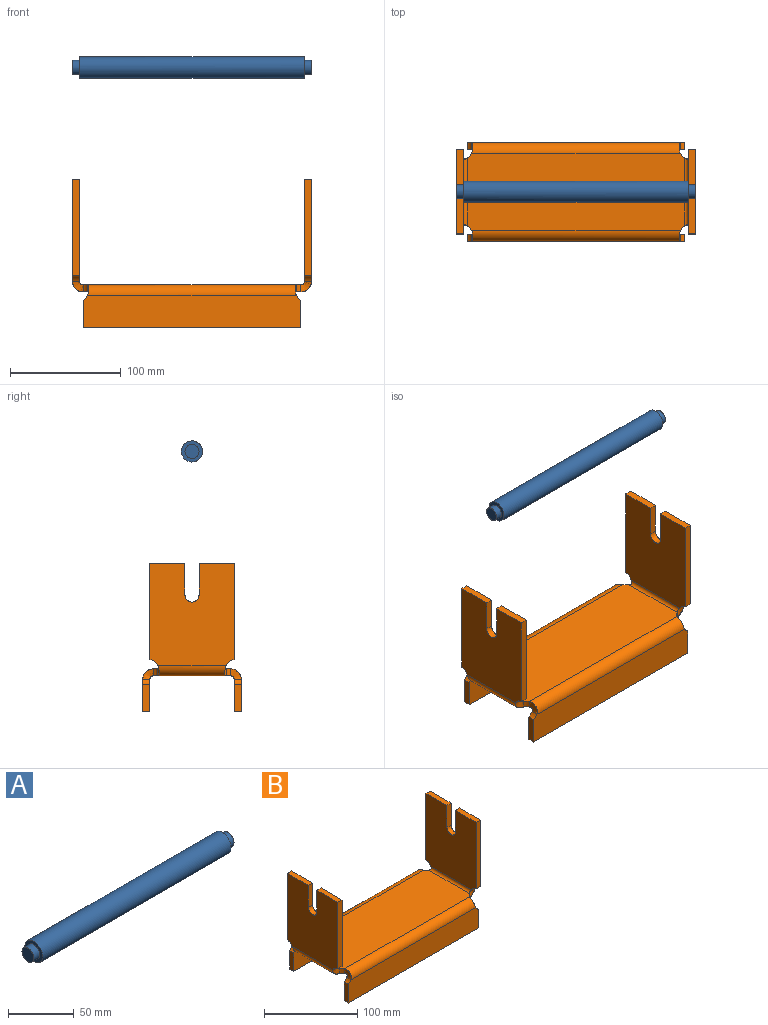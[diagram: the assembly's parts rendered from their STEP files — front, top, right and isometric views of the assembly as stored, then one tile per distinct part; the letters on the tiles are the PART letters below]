
ASSEMBLY  parts=2 mates=3
PART A: 7 faces, bbox 215.9x19.1x19.1 mm
  f0: cylinder r=6.35mm len=12.7mm, axis (-1,0,0), area 253.4mm2, adj f1,f2
  f1: plane 12.7x12.7mm, normal (1,0,0), area 126.7mm2, adj f0
  f2: plane 19.05x19.05mm, normal (1,0,0), area 158.3mm2, adj f0,f4
  f3: plane 19.05x19.05mm, normal (-1,0,0), area 158.3mm2, adj f4,f6
  f4: cylinder r=9.53mm len=203.2mm, axis (-1,0,0), area 12161mm2, adj f2,f3
  f5: plane 12.7x12.7mm, normal (-1,0,0), area 126.7mm2, adj f6
  f6: cylinder r=6.35mm len=12.7mm, axis (-1,0,0), area 253.4mm2, adj f3,f5
PART B: 58 faces, bbox 215.9x88.9x133.4 mm
  f0: plane 31.75x6.35mm, normal (0,0,1), area 201.6mm2, adj f8,f10,f12,f55
  f1: plane 31.75x6.35mm, normal (0,0,1), area 201.6mm2, adj f20,f21,f23,f54
  f2: plane 196.85x69.85mm, normal (0,0,-1), area 13709.2mm2, adj f4,f5,f6,f7,f17,f28,f40,f51
  f3: plane 196.85x69.85mm, normal (0,0,1), area 13709.2mm2, adj f4,f5,f6,f7,f18,f29,f39,f50
  f4: cylinder r=10.05mm len=6.35mm, axis (0,0,1), area 37.6mm2, adj f2,f3,f16,f38
  f5: cylinder r=10.05mm len=6.35mm, axis (0,0,1), area 37.6mm2, adj f2,f3,f27,f37
  f6: cylinder r=10.05mm len=6.35mm, axis (0,0,1), area 37.6mm2, adj f2,f3,f26,f49
  f7: cylinder r=10.05mm len=6.35mm, axis (0,0,1), area 37.6mm2, adj f2,f3,f15,f48
  f8: plane 86.88x6.35mm, normal (0,1,0), area 551.7mm2, adj f0,f10,f12,f13
  f9: plane 86.88x6.35mm, normal (0,-1,0), area 551.7mm2, adj f10,f11,f12,f14
  f10: plane 92.08x76.2mm, normal (-1,0,0), area 6539.3mm2, adj f0,f8,f9,f11,f13,f14,f17,f55
  f11: plane 31.75x6.35mm, normal (0,0,1), area 201.6mm2, adj f9,f10,f12,f56
  f12: plane 92.08x76.2mm, normal (1,0,0), area 6539.3mm2, adj f0,f8,f9,f11,f13,f14,f18,f55
  f13: cylinder r=10.05mm len=7.3mm, axis (1,0,0), area 59mm2, adj f8,f10,f12,f16
  f14: cylinder r=10.05mm len=7.3mm, axis (1,0,0), area 59mm2, adj f9,f10,f12,f15
  f15: bspline ~9.53x9.53mm, area 65.9mm2, adj f7,f14,f17,f18
  f16: bspline ~9.53x9.53mm, area 65.9mm2, adj f4,f13,f17,f18
  f17: cylinder r=9.53mm len=61.6mm, axis (0,-1,0), area 897.6mm2, adj f2,f10,f15,f16
  f18: cylinder r=3.17mm len=61.6mm, axis (0,-1,0), area 299.2mm2, adj f3,f12,f15,f16
  f19: plane 86.88x6.35mm, normal (0,-1,0), area 551.7mm2, adj f21,f22,f23,f24
  f20: plane 86.88x6.35mm, normal (0,1,0), area 551.7mm2, adj f1,f21,f23,f25
  f21: plane 92.08x76.2mm, normal (1,0,0), area 6539.3mm2, adj f1,f19,f20,f22,f24,f25,f28,f52
  f22: plane 31.75x6.35mm, normal (0,0,1), area 201.6mm2, adj f19,f21,f23,f53
  f23: plane 92.08x76.2mm, normal (-1,0,0), area 6539.3mm2, adj f1,f19,f20,f22,f24,f25,f29,f52
  f24: cylinder r=10.05mm len=7.3mm, axis (-1,0,0), area 59mm2, adj f19,f21,f23,f26
  f25: cylinder r=10.05mm len=7.3mm, axis (-1,0,0), area 59mm2, adj f20,f21,f23,f27
  f26: bspline ~9.53x9.53mm, area 65.9mm2, adj f6,f24,f28,f29
  f27: bspline ~9.53x9.53mm, area 65.9mm2, adj f5,f25,f28,f29
  f28: cylinder r=9.53mm len=61.6mm, axis (0,-1,0), area 897.6mm2, adj f2,f21,f26,f27
  f29: cylinder r=3.17mm len=61.6mm, axis (0,-1,0), area 299.2mm2, adj f3,f23,f26,f27
  f30: plane 24.45x6.35mm, normal (1,0,0), area 155.3mm2, adj f32,f33,f34,f35
  f31: plane 24.45x6.35mm, normal (-1,0,0), area 155.3mm2, adj f32,f33,f34,f36
  f32: plane 196.85x28.58mm, normal (0,-1,0), area 5604.6mm2, adj f30,f31,f33,f35,f36,f40
  f33: plane 196.85x6.35mm, normal (0,0,-1), area 1250mm2, adj f30,f31,f32,f34
  f34: plane 196.85x28.58mm, normal (0,1,0), area 5604.6mm2, adj f30,f31,f33,f35,f36,f39
  f35: cylinder r=10.05mm len=6.35mm, axis (0,1,0), area 37.6mm2, adj f30,f32,f34,f37
  f36: cylinder r=10.05mm len=6.35mm, axis (0,1,0), area 37.6mm2, adj f31,f32,f34,f38
  f37: bspline ~9.53x9.53mm, area 65.9mm2, adj f5,f35,f39,f40
  f38: bspline ~9.53x9.53mm, area 65.9mm2, adj f4,f36,f39,f40
  f39: cylinder r=9.53mm len=188.6mm, axis (1,0,0), area 2797.8mm2, adj f3,f34,f37,f38
  f40: cylinder r=3.17mm len=188.6mm, axis (1,0,0), area 932.6mm2, adj f2,f32,f37,f38
  f41: plane 24.45x6.35mm, normal (-1,0,0), area 155.3mm2, adj f43,f44,f45,f46
  f42: plane 24.45x6.35mm, normal (1,0,0), area 155.3mm2, adj f43,f44,f45,f47
  f43: plane 196.85x28.58mm, normal (0,1,0), area 5604.6mm2, adj f41,f42,f44,f46,f47,f51
  f44: plane 196.85x6.35mm, normal (0,0,-1), area 1250mm2, adj f41,f42,f43,f45
  f45: plane 196.85x28.58mm, normal (0,-1,0), area 5604.6mm2, adj f41,f42,f44,f46,f47,f50
  f46: cylinder r=10.05mm len=6.35mm, axis (0,-1,0), area 37.6mm2, adj f41,f43,f45,f48
  f47: cylinder r=10.05mm len=6.35mm, axis (0,-1,0), area 37.6mm2, adj f42,f43,f45,f49
  f48: bspline ~9.53x9.53mm, area 65.9mm2, adj f7,f46,f50,f51
  f49: bspline ~9.53x9.53mm, area 65.9mm2, adj f6,f47,f50,f51
  f50: cylinder r=9.53mm len=188.6mm, axis (-1,0,0), area 2797.8mm2, adj f3,f45,f48,f49
  f51: cylinder r=3.17mm len=188.6mm, axis (-1,0,0), area 932.6mm2, adj f2,f43,f48,f49
  f52: cylinder r=6.35mm len=12.7mm, axis (1,0,0), area 126.7mm2, adj f21,f23,f53,f54
  f53: plane 28.58x6.35mm, normal (0,1,0), area 181.5mm2, adj f21,f22,f23,f52
  f54: plane 28.58x6.35mm, normal (0,-1,0), area 181.5mm2, adj f1,f21,f23,f52
  f55: plane 28.58x6.35mm, normal (0,-1,0), area 181.5mm2, adj f0,f10,f12,f57
  f56: plane 28.58x6.35mm, normal (0,1,0), area 181.5mm2, adj f10,f11,f12,f57
  f57: cylinder r=6.35mm len=12.7mm, axis (1,0,0), area 126.7mm2, adj f10,f12,f55,f56
PLACE A rot(axis=(-1,0,0),149.7deg) t=(0,-33.6,254.08)mm
PLACE B at identity fixed
MATE planar A.f0 <-> B.f10  axis (-1,0,0) through (-107.95,0,196.49)mm
MATE pin_slot A.f0 <-> B.f52  axis (-1,0,0) through (-107.95,0,196.49)mm
MATE parallel A.f0 <-> B.f52  axis (-1,0,0) through (-107.95,0,196.49)mm
